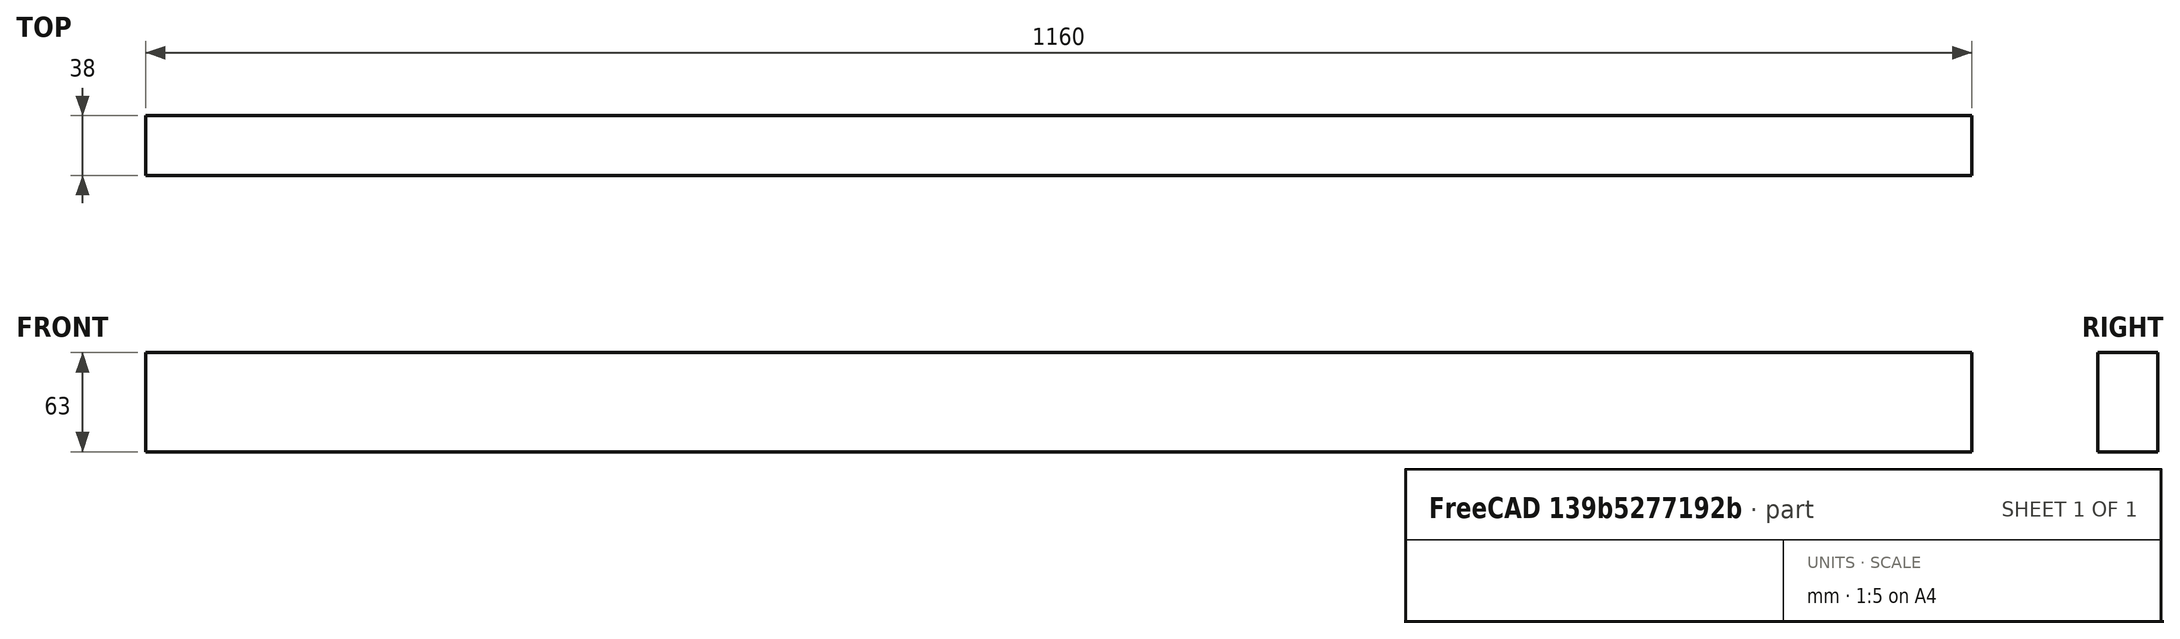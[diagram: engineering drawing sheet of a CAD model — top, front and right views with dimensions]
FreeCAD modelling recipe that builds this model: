
FCSTD DOCUMENT  (FreeCAD 0.21R33771 (Git))
Label: reflector_2024_timber_cut
License: All rights reserved
LicenseURL: https://en.wikipedia.org/wiki/All_rights_reserved
objects: Spreadsheet::Sheet×1, Sketcher::SketchObject×1, PartDesign::Pad×1, PartDesign::Body×1
note: 4 computed .brp shape members not serialized (recipe doc carries the construction recipe); baked Part::Feature solids carry a one-line shape summary decoded from their .brp

FEATURE [Spreadsheet::Sheet] Spreadsheet  label="d"
  cells = A1='width; B1(width)=38; A2='height; B2(height)=63; A3='length; B3(length)=1200; A4='length_cut; B4(length_cut)==1220 - 60
FEATURE [Sketcher::SketchObject] Sketch
  FullyConstrained = true
  MapMode = 5
  Placement = pos=(0,0,0) rot=(0.57735,0.57735,0.57735;2.0944rad)
  Support = -> [YZ_Plane]
  expr: Constraints[5] = <<d>>.width
  expr: Constraints[6] = <<d>>.height
  sketch-geometry (4):
    g0: LineSegment StartX=-19 StartY=31.5 StartZ=0 EndX=19 EndY=31.5 EndZ=0
    g1: LineSegment StartX=19 StartY=31.5 StartZ=0 EndX=19 EndY=-31.5 EndZ=0
    g2: LineSegment StartX=19 StartY=-31.5 StartZ=0 EndX=-19 EndY=-31.5 EndZ=0
    g3: LineSegment StartX=-19 StartY=-31.5 StartZ=0 EndX=-19 EndY=31.5 EndZ=0
  constraints (10):
    c: Coincident(g0,g1)
    c: Coincident(g1,g2)
    c: Coincident(g2,g3)
    c: Coincident(g3,g0)
    c: Horizontal(g2)
    c: DistanceX(g0,g0) = 38
    c: DistanceY(g3,g3) = 63
    c: Symmetric(g0,g0,g-2)
    c: Symmetric(g0,g1,g-1)
    c: Vertical(g3)
FEATURE [PartDesign::Pad] Pad
  Direction = (1,-2e-16,3e-16)
  Length = 1160
  Length2 = 10
  Midplane = true
  Placement = pos=(0,0,0) rot=(1,1,1;2.0944rad)
  Profile = -> Sketch
  ReferenceAxis = -> Sketch [N_Axis]
  Type = 0
  expr: Length = <<d>>.length_cut
FEATURE [PartDesign::Body] Body  label="timber_batten_1160"
  Group = -> [Sketch,Pad]
  Origin = -> Origin
  Tip = -> Pad
